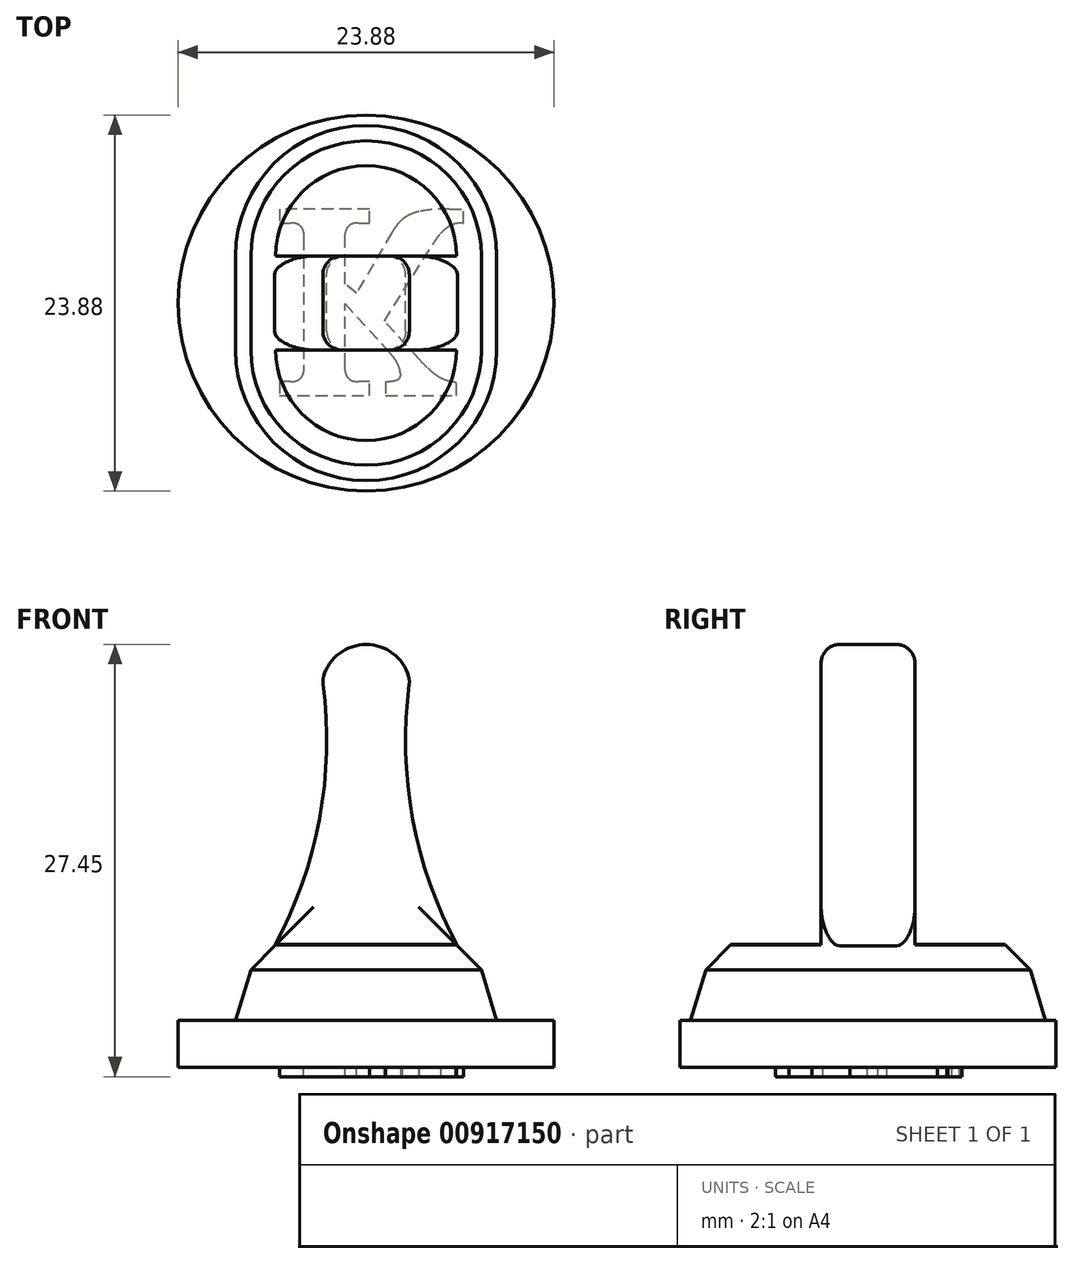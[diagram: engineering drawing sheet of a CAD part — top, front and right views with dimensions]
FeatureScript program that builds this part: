
annotation { "Feature Type Name" : "Feature", "Feature Type Description" : "" }
export const myFeature = defineFeature(function(context is Context, id is Id, definition is map)
    precondition{}
    {
        {
            var Q0;
            Q0=qCreatedBy(makeId("Front.planeOp"),FACE);
            var sketch = newSketch(context, id + "F0", { "sketchPlane" : qUnion([Q0])});
            skLineSegment(sketch, "E0", {"start": v(-24.69, -5.64) * mm, "end": v(-31.15, -12.1) * mm});
            skLineSegment(sketch, "E1.MirrorCS", {"start": v(24.69, -5.64) * mm, "end": v(31.15, -12.1) * mm});
            skLineSegment(sketch, "E2", {"start": v(-31.15, -12.1) * mm, "end": v(31.15, -12.1) * mm});
            skLineSegment(sketch, "E3", {"start": v(-31.15, -12.1) * mm, "end": v(-35.29, -25.8) * mm});
            skLineSegment(sketch, "E4.MirrorCS", {"start": v(31.15, -12.1) * mm, "end": v(35.29, -25.8) * mm});
            skLineSegment(sketch, "E5", {"start": v(-35.29, -25.8) * mm, "end": v(35.29, -25.8) * mm});
            skLineSegment(sketch, "E6", {"start": v(-24.69, -5.64) * mm, "end": v(24.69, -5.64) * mm});
            skArc(sketch, "E7", {"start": v(-24.69, -5.64) * mm, "mid": v(-12.51, 29.13) * mm, "end": v(-11.76, 65.96) * mm});
            skArc(sketch, "E8.MirrorCS", {"start": v(24.69, -5.64) * mm, "mid": v(12.51, 29.13) * mm, "end": v(11.76, 65.96) * mm});
            skArc(sketch, "E9", {"start": v(11.76, 65.96) * mm, "mid": v(0, 75.8) * mm, "end": v(-11.76, 65.96) * mm});
            skSolve(sketch);
        }
        {
            var Q0;
            Q0=qSketchRegion(id+"F0",true);
            extrude(context, id + "F1", {"entities" : qUnion([Q0]), "endBound" : BoundingType.SYMMETRIC, "depth" : 25.4 * mm, "offsetDistance" : 25.4 * mm});
        }
        {
            var Q0;
            Q0=makeQuery(id+"F1.opExtrude","CAP_EDGE",EDGE,{"disambiguationData":[OSD([sQuery(id+"F0.wireOp",EDGE,"E8.MirrorCS")])],"isStart":false});
            var Q1;
            Q1=makeQuery(id+"F1.opExtrude","CAP_EDGE",EDGE,{"disambiguationData":[OSD([sQuery(id+"F0.wireOp",EDGE,"E7")])],"isStart":false});
            var Q2;
            Q2=makeQuery(id+"F1.opExtrude","CAP_EDGE",EDGE,{"disambiguationData":[OSD([sQuery(id+"F0.wireOp",EDGE,"E8.MirrorCS")])],"isStart":true});
            var Q3;
            Q3=makeQuery(id+"F1.opExtrude","CAP_EDGE",EDGE,{"disambiguationData":[OSD([sQuery(id+"F0.wireOp",EDGE,"E7")])],"isStart":true});
            var Q4;
            Q4=makeQuery(id+"F1.opExtrude","SWEPT_FACE",FACE,{"disambiguationData":[OSD([sQuery(id+"F0.wireOp",EDGE,"E9")])]});
            fillet(context, id + "F2", {"entities" : qUnion([Q0, Q1, Q2, Q3, Q4]), "radius" : 5.08 * mm, "tangentPropagation" : true, "allowEdgeOverflow" : false});
        }
        {
            var Q0;
            Q0=makeQuery(id+"F1.opExtrude","SWEPT_FACE",FACE,{"disambiguationData":[OSD([sQuery(id+"F0.wireOp",EDGE,"E5")])]});
            var sketch = newSketch(context, id + "F3", { "sketchPlane" : qUnion([Q0])});
            skCircle(sketch, "E10", {"center": v(0, 0) * mm, "radius": 50.8 * mm});
            skSolve(sketch);
        }
        {
            var Q0;
            Q0=makeQuery(id+"F3.imprint","IMPRINT",FACE,{"disambiguationData":[TD([[makeQuery(id+"F3.imprint","IMPRINT",EDGE,{"derivedFrom":sQuery(id+"F3.wireOp",EDGE,"E10")}),1.0]])]});
            var Q1;
            {var subQ0=sQuery(id+"F0.wireOp",EDGE,"E5");Q1=makeQuery(id+"F3.imprint","IMPRINT",FACE,{"disambiguationData":[TD([[makeQuery(id+"F3.imprint","IMPRINT",EDGE,{"derivedFrom":makeQuery(id+"F1.opExtrude","CAP_EDGE",EDGE,{"disambiguationData":[OSD([subQ0])],"isStart":true})}),1.0]])]});}
            var Q2;
            Q2=sQuery(id+"F3.wireOp",EDGE,"E10");
            extrude(context, id + "F4", {"entities" : qUnion([Q0, Q1]), "operationType" : NewBodyOperationType.ADD, "surfaceEntities" : qUnion([Q2]), "depth" : 12.7 * mm, "offsetDistance" : 25.4 * mm});
        }
        {
            var Q0;
            Q0=makeQuery(id+"F4.opExtrude","CAP_FACE",FACE,{"disambiguationData":[OSD([sQuery(id+"F3.wireOp",EDGE,"E10")])],"isStart":false});
            var sketch = newSketch(context, id + "F5", { "sketchPlane" : qUnion([Q0])});
            skLineSegment(sketch, "E11.top", {"start": v(0, -25.4) * mm, "end": v(30.96, -25.4) * mm});
            skLineSegment(sketch, "E11.right", {"start": v(30.96, 0) * mm, "end": v(30.96, -25.4) * mm});
            skLineSegment(sketch, "E12.top", {"start": v(0, -25.4) * mm, "end": v(-25.4, -25.4) * mm});
            skLineSegment(sketch, "E12.right", {"start": v(-25.4, 0) * mm, "end": v(-25.4, -25.4) * mm});
            skPoint(sketch, "E13.oppositeSnap0", {"position": v(-25.4, -12.7) * mm});
            skLineSegment(sketch, "E13.top", {"start": v(0, 25.4) * mm, "end": v(-25.4, 25.4) * mm});
            skLineSegment(sketch, "E13.right", {"start": v(-25.4, 0) * mm, "end": v(-25.4, 25.4) * mm});
            skLineSegment(sketch, "E14.bottom", {"start": v(0, 25.4) * mm, "end": v(25.56, 25.4) * mm});
            skText(sketch, "E15", { "text": "K\n", "fontName": "NotoSerif-Bold.ttf"});
            const initialGuessF5  = {"E15": [-0.0254, -0.0254, 1, 0, 0.0508]};
            skSetInitialGuess(sketch, initialGuessF5);
            skSolve(sketch);
        }
        {
            var Q0;
            Q0=makeQuery(id+"F5.imprint","IMPRINT",FACE,{"disambiguationData":[TD([[makeQuery(id+"F5.imprint","IMPRINT",EDGE,{"derivedFrom":sQuery(id+"F5.wireOp",EDGE,"E15.sketch_text.stroke-0")}),-1.0]])]});
            extrude(context, id + "F6", {"entities" : qUnion([Q0]), "operationType" : NewBodyOperationType.ADD, "depth" : 2.54 * mm, "offsetDistance" : 25.4 * mm});
        }
        {
            var Q0;
            Q0=makeQuery(id+"F1.opExtrude","SWEPT_BODY",BODY,{"disambiguationData":[OSD([sQuery(id+"F0.wireOp",EDGE,"E0"),sQuery(id+"F0.wireOp",EDGE,"E1.MirrorCS"),sQuery(id+"F0.wireOp",EDGE,"E3"),sQuery(id+"F0.wireOp",EDGE,"E4.MirrorCS"),sQuery(id+"F0.wireOp",EDGE,"E5"),sQuery(id+"F0.wireOp",EDGE,"E7"),sQuery(id+"F0.wireOp",EDGE,"E8.MirrorCS"),sQuery(id+"F0.wireOp",EDGE,"E9")])]});
            var Q1;
            Q1=qCreatedBy(makeId("Origin.pointOp"),VERTEX);
            transform(context, id + "F7", {"entities" : qUnion([Q0]), "transformType" : TransformType.SCALE_UNIFORMLY, "scale" : 0.23, "scalePoint" : qUnion([Q1]), "makeCopy" : false});
        }
        {
            var Q0;
            Q0=makeQuery(id+"F1.opExtrude","CAP_FACE",FACE,{"disambiguationData":[OSD([sQuery(id+"F0.wireOp",EDGE,"E0"),sQuery(id+"F0.wireOp",EDGE,"E1.MirrorCS"),sQuery(id+"F0.wireOp",EDGE,"E3"),sQuery(id+"F0.wireOp",EDGE,"E4.MirrorCS"),sQuery(id+"F0.wireOp",EDGE,"E5"),sQuery(id+"F0.wireOp",EDGE,"E7"),sQuery(id+"F0.wireOp",EDGE,"E8.MirrorCS"),sQuery(id+"F0.wireOp",EDGE,"E9")])],"isStart":true});
            var sketch = newSketch(context, id + "F8", { "sketchPlane" : qUnion([Q0])});
            skLineSegment(sketch, "E16", {"start": v(-5.74, -1.27) * mm, "end": v(-5.74, -6.06) * mm});
            skLineSegment(sketch, "E17", {"start": v(-5.74, -1.27) * mm, "end": v(-7.32, -2.84) * mm});
            skLineSegment(sketch, "E18", {"start": v(-7.32, -2.84) * mm, "end": v(-8.3, -6.06) * mm});
            skLineSegment(sketch, "E19", {"start": v(-8.3, -6.06) * mm, "end": v(-5.74, -6.06) * mm});
            skLineSegment(sketch, "E20", {"start": v(0, 0) * mm, "end": v(0, -6.06) * mm, "construction": true});
            skSolve(sketch);
        }
        {
            var Q0;
            Q0=makeQuery(id+"F1.opExtrude","CAP_FACE",FACE,{"disambiguationData":[OSD([sQuery(id+"F0.wireOp",EDGE,"E0"),sQuery(id+"F0.wireOp",EDGE,"E1.MirrorCS"),sQuery(id+"F0.wireOp",EDGE,"E3"),sQuery(id+"F0.wireOp",EDGE,"E4.MirrorCS"),sQuery(id+"F0.wireOp",EDGE,"E5"),sQuery(id+"F0.wireOp",EDGE,"E7"),sQuery(id+"F0.wireOp",EDGE,"E8.MirrorCS"),sQuery(id+"F0.wireOp",EDGE,"E9")])],"isStart":false});
            var sketch = newSketch(context, id + "F9", { "sketchPlane" : qUnion([Q0])});
            skLineSegment(sketch, "E21", {"start": v(0, 0.3) * mm, "end": v(0, -6.06) * mm, "construction": true});
            skLineSegment(sketch, "E22.0.0", {"start": v(5.74, -6.06) * mm, "end": v(5.74, -1.27) * mm});
            skLineSegment(sketch, "E22.0.1", {"start": v(5.74, -1.27) * mm, "end": v(7.32, -2.84) * mm});
            skLineSegment(sketch, "E22.0.2", {"start": v(7.32, -2.84) * mm, "end": v(8.3, -6.06) * mm});
            skLineSegment(sketch, "E22.0.3", {"start": v(8.3, -6.06) * mm, "end": v(5.74, -6.06) * mm});
            skSolve(sketch);
        }
        {
            var Q0;
            Q0=makeQuery(id+"F8.imprint","IMPRINT",FACE,{"disambiguationData":[TD([[makeQuery(id+"F8.imprint","IMPRINT",EDGE,{"derivedFrom":sQuery(id+"F8.wireOp",EDGE,"E16")}),-1.0]])]});
            var Q1;
            Q1=sQuery(id+"F8.wireOp",EDGE,"E20");
            revolve(context, id + "F10", {"operationType" : NewBodyOperationType.ADD, "surfaceOperationType" : NewSurfaceOperationType.NEW, "entities" : qUnion([Q0]), "axis" : qUnion([Q1]), "revolveType" : RevolveType.ONE_DIRECTION, "oppositeDirection" : true, "angle" : 180 * degree});
        }
        {
            var Q0;
            Q0=makeQuery(id+"F9.imprint","IMPRINT",FACE,{"disambiguationData":[TD([[makeQuery(id+"F9.imprint","IMPRINT",EDGE,{"derivedFrom":sQuery(id+"F9.wireOp",EDGE,"E22.0.0")}),-1.0]])]});
            var Q1;
            Q1=sQuery(id+"F9.wireOp",EDGE,"E21");
            revolve(context, id + "F11", {"operationType" : NewBodyOperationType.ADD, "surfaceOperationType" : NewSurfaceOperationType.NEW, "entities" : qUnion([Q0]), "axis" : qUnion([Q1]), "revolveType" : RevolveType.ONE_DIRECTION, "angle" : 180 * degree});
        }
        {
            var Q0;
            {var subQ1=sQuery(id+"F0.wireOp",EDGE,"E3");var subQ3=sQuery(id+"F3.wireOp",EDGE,"E10");Q0=makeQuery(id+"F11.boolean.opBoolean","SPLIT",FACE,{"disambiguationData":[TD([makeQuery(id+"F11.opRevolve","SWEPT_FACE",FACE,{"disambiguationData":[OSD([sQuery(id+"F9.wireOp",EDGE,"E22.0.0")])]})])],"derivedFrom":makeQuery(id+"F10.boolean.opBoolean","SPLIT",FACE,{"disambiguationData":[TD([makeQuery(id+"F1.opExtrude","SWEPT_FACE",FACE,{"disambiguationData":[OSD([subQ1])]})])],"derivedFrom":makeQuery(id+"F4.opExtrude","CAP_FACE",FACE,{"disambiguationData":[OSD([subQ3])],"isStart":true})})});}
            extrude(context, id + "F12", {"entities" : qUnion([Q0]), "operationType" : NewBodyOperationType.ADD, "depth" : 4.83 * mm, "offsetDistance" : 25.4 * mm});
        }
        {
            var Q0;
            Q0=makeQuery(id+"F10.boolean.opBoolean","SPLIT",FACE,{"disambiguationData":[TD([makeQuery(id+"F10.opRevolve","SWEPT_FACE",FACE,{"disambiguationData":[OSD([sQuery(id+"F8.wireOp",EDGE,"E16")])]})])],"derivedFrom":makeQuery(id+"F4.opExtrude","CAP_FACE",FACE,{"disambiguationData":[OSD([sQuery(id+"F3.wireOp",EDGE,"E10")])],"isStart":true})});
            extrude(context, id + "F13", {"entities" : qUnion([Q0]), "operationType" : NewBodyOperationType.ADD, "depth" : 4.83 * mm, "offsetDistance" : 25.4 * mm});
        }
        {
            var Q0;
            {var subQ0=sQuery(id+"F0.wireOp",EDGE,"E9");Q0=makeQuery(id+"F2.opFillet","BLEND_EDGE",EDGE,{"blendedFrom":[makeQuery(id+"F1.opExtrude","CAP_EDGE",EDGE,{"disambiguationData":[OSD([subQ0])],"isStart":false}),makeQuery(id+"F1.opExtrude","CAP_FACE",FACE,{"disambiguationData":[OSD([sQuery(id+"F0.wireOp",EDGE,"E0"),sQuery(id+"F0.wireOp",EDGE,"E1.MirrorCS"),sQuery(id+"F0.wireOp",EDGE,"E3"),sQuery(id+"F0.wireOp",EDGE,"E4.MirrorCS"),sQuery(id+"F0.wireOp",EDGE,"E5"),sQuery(id+"F0.wireOp",EDGE,"E7"),sQuery(id+"F0.wireOp",EDGE,"E8.MirrorCS"),subQ0])],"isStart":false})],"blendedInto":[makeQuery(id+"F1.opExtrude","CAP_FACE",FACE,{"disambiguationData":[OSD([sQuery(id+"F0.wireOp",EDGE,"E0"),sQuery(id+"F0.wireOp",EDGE,"E1.MirrorCS"),sQuery(id+"F0.wireOp",EDGE,"E3"),sQuery(id+"F0.wireOp",EDGE,"E4.MirrorCS"),sQuery(id+"F0.wireOp",EDGE,"E5"),sQuery(id+"F0.wireOp",EDGE,"E7"),sQuery(id+"F0.wireOp",EDGE,"E8.MirrorCS"),subQ0])],"isStart":false})]});}
            var Q1;
            {var subQ0=sQuery(id+"F0.wireOp",EDGE,"E8.MirrorCS");Q1=makeQuery(id+"F2.opFillet","BLEND_EDGE",EDGE,{"blendedFrom":[makeQuery(id+"F1.opExtrude","SWEPT_EDGE",EDGE,{"disambiguationData":[OSD([subQ0,sQuery(id+"F0.wireOp",EDGE,"E9")])]}),makeQuery(id+"F1.opExtrude","SWEPT_FACE",FACE,{"disambiguationData":[OSD([subQ0])]})],"blendedInto":[makeQuery(id+"F1.opExtrude","SWEPT_FACE",FACE,{"disambiguationData":[OSD([subQ0])]})]});}
            cPlane(context, id + "F14", {"entities" : qUnion([Q0, Q1]), "cplaneType" : CPlaneType.LINE_ANGLE, "offset" : 25.4 * mm, "angle" : 0 * degree, "width" : 152.4 * mm, "height" : 152.4 * mm});
        }
    });
